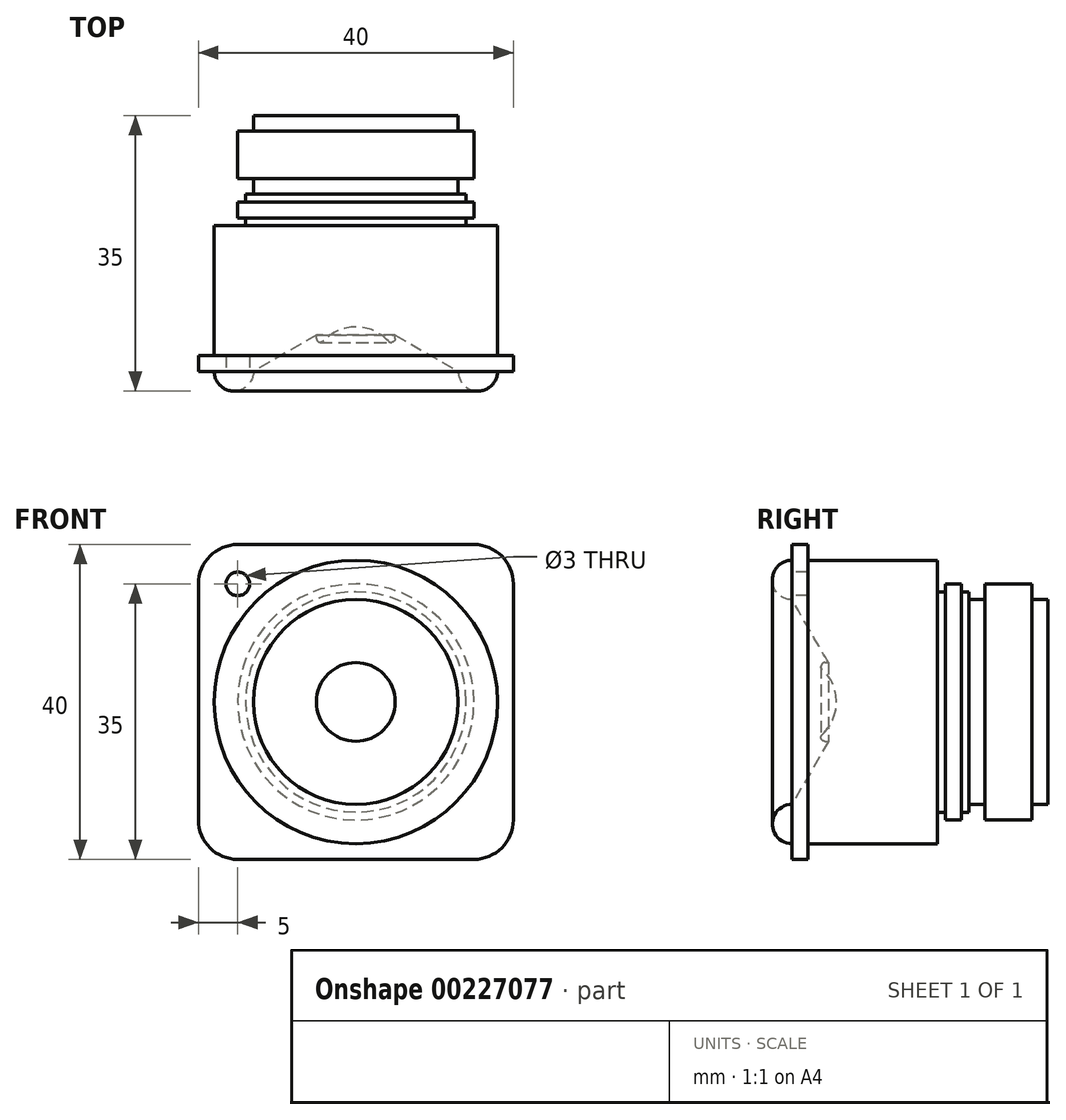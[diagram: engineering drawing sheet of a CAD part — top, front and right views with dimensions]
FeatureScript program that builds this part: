
annotation { "Feature Type Name" : "Feature", "Feature Type Description" : "" }
export const myFeature = defineFeature(function(context is Context, id is Id, definition is map)
    precondition{}
    {
        {
            var Q0;
            Q0=qCreatedBy(makeId("Front.planeOp"),FACE);
            var sketch = newSketch(context, id + "F0", { "sketchPlane" : qUnion([Q0])});
            skLineSegment(sketch, "E0.bottom", {"start": v(20, -20) * mm, "end": v(-20, -20) * mm});
            skLineSegment(sketch, "E0.top", {"start": v(20, 20) * mm, "end": v(-20, 20) * mm});
            skLineSegment(sketch, "E0.left", {"start": v(20, -20) * mm, "end": v(20, 20) * mm});
            skLineSegment(sketch, "E0.right", {"start": v(-20, -20) * mm, "end": v(-20, 20) * mm});
            skPoint(sketch, "E0.middle", {"position": v(0, 0) * mm});
            skSolve(sketch);
        }
        {
            var Q0;
            Q0=makeQuery(id+"F0.imprint","IMPRINT",FACE,{"disambiguationData":[TD([[makeQuery(id+"F0.imprint","IMPRINT",EDGE,{"derivedFrom":sQuery(id+"F0.wireOp",EDGE,"E0.bottom")}),-1.0]])]});
            extrude(context, id + "F1", {"entities" : qUnion([Q0]), "oppositeDirection" : true, "depth" : 2 * mm});
        }
        {
            var Q0;
            Q0=makeQuery(id+"F1.opExtrude","SWEPT_EDGE",EDGE,{"disambiguationData":[OSD([sQuery(id+"F0.wireOp",EDGE,"E0.top"),sQuery(id+"F0.wireOp",EDGE,"E0.left")])]});
            var Q1;
            Q1=makeQuery(id+"F1.opExtrude","SWEPT_EDGE",EDGE,{"disambiguationData":[OSD([sQuery(id+"F0.wireOp",EDGE,"E0.bottom"),sQuery(id+"F0.wireOp",EDGE,"E0.left")])]});
            var Q2;
            Q2=makeQuery(id+"F1.opExtrude","SWEPT_EDGE",EDGE,{"disambiguationData":[OSD([sQuery(id+"F0.wireOp",EDGE,"E0.bottom"),sQuery(id+"F0.wireOp",EDGE,"E0.right")])]});
            var Q3;
            Q3=makeQuery(id+"F1.opExtrude","SWEPT_EDGE",EDGE,{"disambiguationData":[OSD([sQuery(id+"F0.wireOp",EDGE,"E0.top"),sQuery(id+"F0.wireOp",EDGE,"E0.right")])]});
            fillet(context, id + "F2", {"entities" : qUnion([Q0, Q1, Q2, Q3]), "radius" : 5 * mm, "tangentPropagation" : true, "allowEdgeOverflow" : false});
        }
        {
            var Q0;
            Q0=makeQuery(id+"F1.opExtrude","CAP_FACE",FACE,{"disambiguationData":[OSD([sQuery(id+"F0.wireOp",EDGE,"E0.bottom"),sQuery(id+"F0.wireOp",EDGE,"E0.top"),sQuery(id+"F0.wireOp",EDGE,"E0.left"),sQuery(id+"F0.wireOp",EDGE,"E0.right")])],"isStart":true});
            var sketch = newSketch(context, id + "F3", { "sketchPlane" : qUnion([Q0])});
            skCircle(sketch, "E1", {"center": v(0, 0) * mm, "radius": 18 * mm});
            skSolve(sketch);
        }
        {
            var Q0;
            Q0 = qSketchRegion(id + "F3", true);
            extrude(context, id + "F4", {"entities" : qUnion([Q0]), "operationType" : NewBodyOperationType.REMOVE, "endBound" : BoundingType.UP_TO_NEXT, "oppositeDirection" : true, "depth" : 25 * mm});
        }
        {
            var Q0;
            Q0=qCreatedBy(makeId("Right.planeOp"),FACE);
            var sketch = newSketch(context, id + "F5", { "sketchPlane" : qUnion([Q0])});
            skLineSegment(sketch, "E2", {"start": v(0, 18) * mm, "end": v(-2.5, 18) * mm});
            skLineSegment(sketch, "E3", {"start": v(-2.5, 18) * mm, "end": v(-2.5, 13) * mm});
            skLineSegment(sketch, "E4", {"start": v(-2.5, 13) * mm, "end": v(0, 13) * mm});
            skLineSegment(sketch, "E5", {"start": v(0, 13) * mm, "end": v(4.62, 5) * mm});
            skLineSegment(sketch, "E6", {"start": v(4.62, 5) * mm, "end": v(2.62, 5) * mm});
            skArc(sketch, "E7", {"start": v(5.64, 0) * mm, "mid": v(4.83, 2.92) * mm, "end": v(2.62, 5) * mm});
            skLineSegment(sketch, "E8", {"start": v(0, 18) * mm, "end": v(18.5, 18) * mm});
            skLineSegment(sketch, "E9", {"start": v(18.5, 18) * mm, "end": v(18.5, 14) * mm});
            skLineSegment(sketch, "E10", {"start": v(18.5, 14) * mm, "end": v(19.5, 14) * mm});
            skLineSegment(sketch, "E11", {"start": v(19.5, 14) * mm, "end": v(19.5, 15) * mm});
            skLineSegment(sketch, "E12", {"start": v(19.5, 15) * mm, "end": v(21.5, 15) * mm});
            skLineSegment(sketch, "E13", {"start": v(21.5, 15) * mm, "end": v(21.5, 14) * mm});
            skLineSegment(sketch, "E14", {"start": v(21.5, 14) * mm, "end": v(22.5, 14) * mm});
            skLineSegment(sketch, "E15", {"start": v(22.5, 13) * mm, "end": v(22.5, 14) * mm});
            skLineSegment(sketch, "E16", {"start": v(22.5, 13) * mm, "end": v(24.5, 13) * mm});
            skLineSegment(sketch, "E17", {"start": v(24.5, 13) * mm, "end": v(24.5, 15) * mm});
            skLineSegment(sketch, "E18", {"start": v(24.5, 15) * mm, "end": v(30.5, 15) * mm});
            skLineSegment(sketch, "E19", {"start": v(30.5, 15) * mm, "end": v(30.5, 13) * mm});
            skPoint(sketch, "E19.endSnap0", {"position": v(23.5, 13) * mm});
            skLineSegment(sketch, "E20", {"start": v(30.5, 13) * mm, "end": v(32.5, 13) * mm});
            skLineSegment(sketch, "E21", {"start": v(32.5, 13) * mm, "end": v(32.5, 0) * mm});
            skLineSegment(sketch, "E22", {"start": v(32.5, 0) * mm, "end": v(5.64, 0) * mm});
            skSolve(sketch);
        }
        {
            var Q0;
            Q0=makeQuery(id+"F5.imprint","IMPRINT",FACE,{"disambiguationData":[TD([[makeQuery(id+"F5.imprint","IMPRINT",EDGE,{"derivedFrom":sQuery(id+"F5.wireOp",EDGE,"E2")}),1.0]])]});
            var Q1;
            Q1=sQuery(id+"F5.wireOp",EDGE,"E22");
            revolve(context, id + "F6", {"operationType" : NewBodyOperationType.ADD, "entities" : qUnion([Q0]), "axis" : qUnion([Q1]), "revolveType" : RevolveType.FULL});
        }
        {
            var Q0;
            Q0=makeQuery(id+"F6.opRevolve","SWEPT_EDGE",EDGE,{"disambiguationData":[OSD([sQuery(id+"F5.wireOp",EDGE,"E2"),sQuery(id+"F5.wireOp",EDGE,"E3")])]});
            var Q1;
            Q1=makeQuery(id+"F6.opRevolve","SWEPT_EDGE",EDGE,{"disambiguationData":[OSD([sQuery(id+"F5.wireOp",EDGE,"E3"),sQuery(id+"F5.wireOp",EDGE,"E4")])]});
            fillet(context, id + "F7", {"entities" : qUnion([Q0, Q1]), "radius" : 2.5 * mm, "tangentPropagation" : true, "allowEdgeOverflow" : false});
        }
        {
            var Q0;
            Q0=makeQuery(id+"F6.opRevolve","SWEPT_EDGE",EDGE,{"disambiguationData":[OSD([sQuery(id+"F5.wireOp",EDGE,"E6"),sQuery(id+"F5.wireOp",EDGE,"E7")])]});
            fillet(context, id + "F8", {"entities" : qUnion([Q0]), "radius" : 0.5 * mm, "tangentPropagation" : true, "allowEdgeOverflow" : false});
        }
        {
            var Q0;
            Q0=qCreatedBy(makeId("Front.planeOp"),FACE);
            var sketch = newSketch(context, id + "F9", { "sketchPlane" : qUnion([Q0])});
            skArc(sketch, "E23.0", {"start": v(-15, 20) * mm, "mid": v(-18.54, 18.54) * mm, "end": v(-20, 15) * mm, "construction": true});
            skSolve(sketch);
        }
        {
            var Q0;
            Q0=sQuery(id+"F9.wireOp",VERTEX,"E23.0.center");
            var Q1;
            Q1=makeQuery(id+"F1.opExtrude","SWEPT_BODY",BODY,{"disambiguationData":[OSD([sQuery(id+"F0.wireOp",EDGE,"E0.bottom"),sQuery(id+"F0.wireOp",EDGE,"E0.top"),sQuery(id+"F0.wireOp",EDGE,"E0.left"),sQuery(id+"F0.wireOp",EDGE,"E0.right")])]});
            hole(context, id + "F10", {"style" : HoleStyle.SIMPLE, "endStyle" : HoleEndStyle.THROUGH, "holeDiameter" : 3 * mm, "locations" : qUnion([Q0]), "scope" : qUnion([Q1]), "isTappedThrough" : true});
        }
    });
